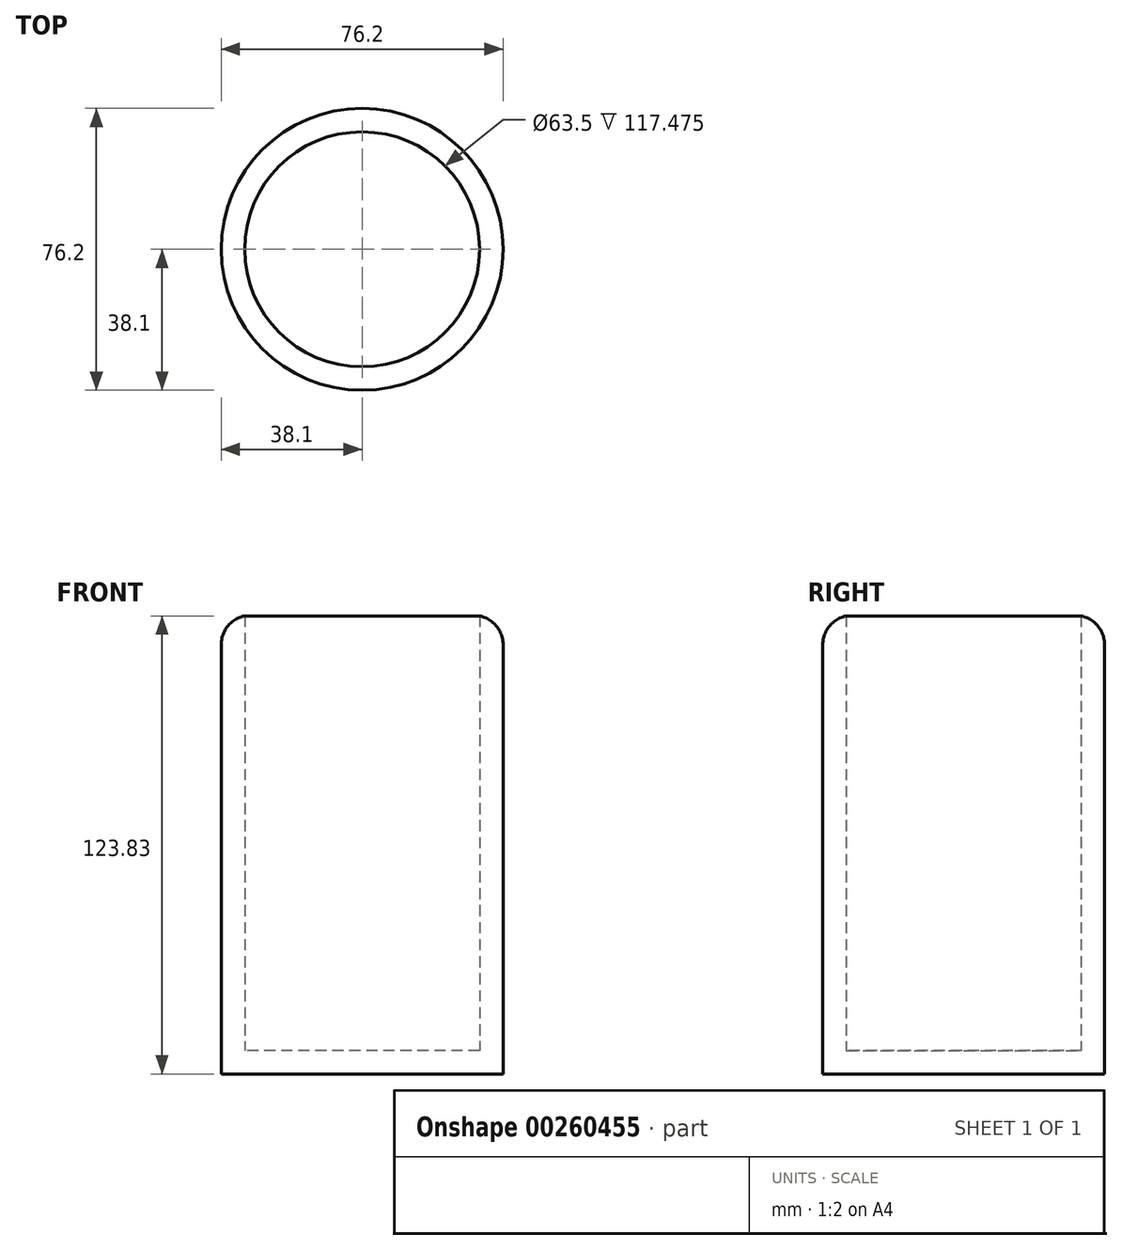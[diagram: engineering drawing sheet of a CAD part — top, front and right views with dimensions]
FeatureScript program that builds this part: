
annotation { "Feature Type Name" : "Feature", "Feature Type Description" : "" }
export const myFeature = defineFeature(function(context is Context, id is Id, definition is map)
    precondition{}
    {
        {
            var Q0;
            Q0=qCreatedBy(makeId("Top.planeOp"),FACE);
            var sketch = newSketch(context, id + "F0", { "sketchPlane" : qUnion([Q0])});
            skCircle(sketch, "E0", {"center": v(0, 0) * mm, "radius": 38.1 * mm});
            skSolve(sketch);
        }
        {
            var Q0;
            Q0 = qSketchRegion(id + "F0", true);
            extrude(context, id + "F1", {"entities" : qUnion([Q0]), "depth" : 123.82 * mm});
        }
        {
            var Q0;
            Q0=makeQuery(id+"F1.opExtrude","CAP_FACE",FACE,{"disambiguationData":[OSD([sQuery(id+"F0.wireOp",EDGE,"E0")])],"isStart":false});
            shell(context, id + "F2", {"entities" : qUnion([Q0]), "thickness" : 6.35 * mm});
        }
        {
            var Q0;
            Q0=makeQuery(id+"F1.opExtrude","CAP_EDGE",EDGE,{"disambiguationData":[OSD([sQuery(id+"F0.wireOp",EDGE,"E0")])],"isStart":false});
            fillet(context, id + "F3", {"entities" : qUnion([Q0]), "radius" : 7.97 * mm, "tangentPropagation" : true, "allowEdgeOverflow" : false});
        }
    });
